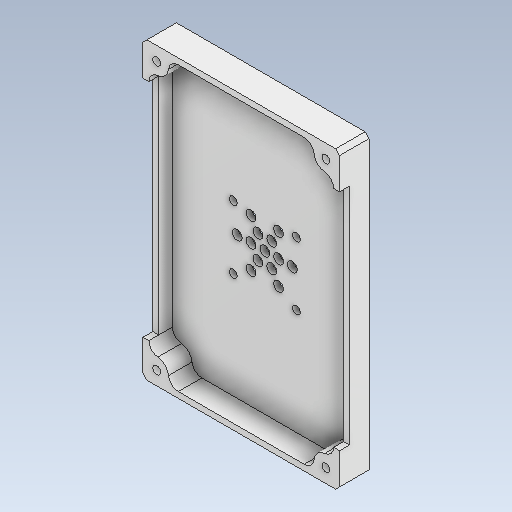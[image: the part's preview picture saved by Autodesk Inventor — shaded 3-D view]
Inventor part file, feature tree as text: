
AUTODESK INVENTOR PART (.ipt)
format: ipt  version: 2020 (Build 240168000, 168)  size: 240,640 bytes
history: native  units: mm
features: sketch x7, extrude x5, reference x5, other x4, hole x2, projected_geometry x2, fillet x1, chamfer x1, pattern_circular x1
ambient origin geometry x8: Origin, YZ Plane, XZ Plane, XY Plane, X Axis, Y Axis, Z Axis, Center Point
bodies: Solid1 (feature_tree)
feature tree (28):
  extrude  "Extrusion1"  Depth=150.0mm
  extrude  "Extrusion2"  Depth=3.0mm
  hole  "Hole1"  [1 undecoded]
  extrude  "Extrusion3"  Depth=4.0mm
  fillet  "Fillet1"  Radius=27.0mm
  extrude  "Extrusion5"  Depth=10.0mm
  chamfer  "Chamfer1"  Distance=50.0mm
  hole  "Hole2"  [1 undecoded]
  extrude  "Extrusion6"  Depth=7.0mm
  pattern_circular  "Circular Pattern1"  [2 undecoded]
  sketch  "Sketch1"  dims[d0=100.0mm d1=150.0mm]
  sketch  "Sketch2"  dims[d2=15.0mm d3=0.0mm d4=3.0mm]
  projected_geometry  "Projected Loop1"
  sketch  "Sketch3"  dims[d5=12.0mm d6=0.0mm]
  sketch  "Sketch4"  dims[d9=4.0mm d10=6.0mm d11=4.0mm d12=2.0mm d13=90.0deg d14=8.0mm d15=20.594885mm d16=12.0mm]
  projected_geometry  "Projected Loop2"
  sketch  "Sketch6"  dims[d17=4.0mm d18=4.0mm d19=27.0mm d20=0.0mm]
  sketch  "Sketch7"  dims[d21=5.0mm d24=10.0mm d25=50.0mm d26=0.0mm]
  reference  "Reference1"
  reference  "Reference2"
  reference  "Reference3"
  reference  "Reference4"
  reference  "Reference5"
  sketch  "Sketch8"  dims[d27=2.0mm d28=2.0mm d29=45.0deg d30=4.0mm d31=6.0mm d32=4.0mm d33=2.0mm d34=90.0deg d35=8.0mm d36=20.594885mm d37=5.0mm d38=7.0mm d39=7.0mm d40=10.0mm d41=0.0mm d42=60.0mm d43=360.0deg]
  other  "<path> 2.1 Aracet_Subansamble.iam"
  other  "I.A.B 2.1 Aracet_Subansamble.iam"
  other  "0008-10-027 Cutie Arduino:1"
  other  "008-20-1010 NF-A4x10_Noctua_40mm:1"
note: 4 required parameter values undecoded (feature->parameter linkage not recoverable at this tier; creation-order binding heuristic only, values carry confidence <= 0.55)
note: 1 file-system path scrubbed to <path> (originals preserved in map.json)
